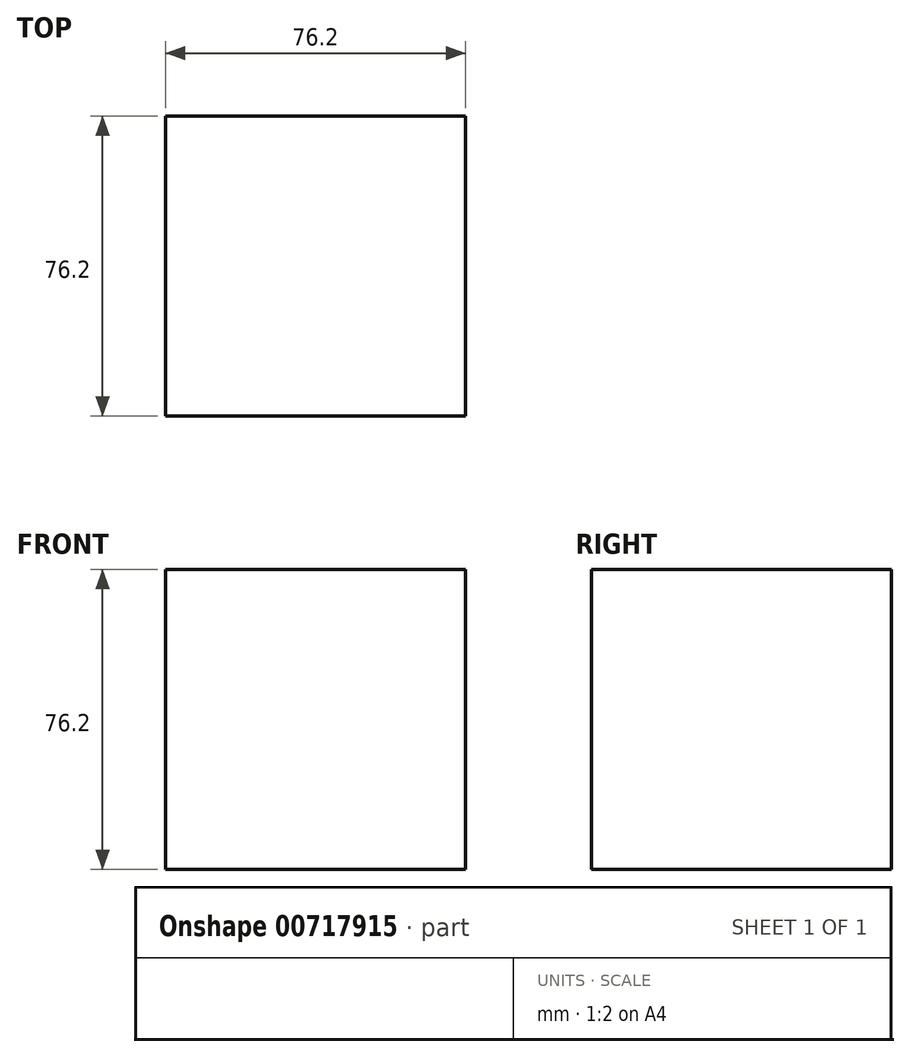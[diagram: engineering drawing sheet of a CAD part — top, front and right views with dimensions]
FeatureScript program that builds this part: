
annotation { "Feature Type Name" : "Feature", "Feature Type Description" : "" }
export const myFeature = defineFeature(function(context is Context, id is Id, definition is map)
    precondition{}
    {
        {
            var Q0;
            Q0=qCreatedBy(makeId("Front.planeOp"),FACE);
            var sketch = newSketch(context, id + "F0", { "sketchPlane" : qUnion([Q0])});
            skLineSegment(sketch, "E0.bottom", {"start": v(-25.54, 34.9) * mm, "end": v(50.66, 34.9) * mm});
            skLineSegment(sketch, "E0.top", {"start": v(-25.54, -41.3) * mm, "end": v(50.66, -41.3) * mm});
            skLineSegment(sketch, "E0.left", {"start": v(-25.54, 34.9) * mm, "end": v(-25.54, -41.3) * mm});
            skLineSegment(sketch, "E0.right", {"start": v(50.66, 34.9) * mm, "end": v(50.66, -41.3) * mm});
            skSolve(sketch);
        }
        {
            var Q0;
            Q0=makeQuery(id+"F0.imprint","IMPRINT",FACE,{"disambiguationData":[TD([[makeQuery(id+"F0.imprint","IMPRINT",EDGE,{"derivedFrom":sQuery(id+"F0.wireOp",EDGE,"E0.bottom")}),-1.0]])]});
            extrude(context, id + "F1", {"entities" : qUnion([Q0]), "depth" : 76.2 * mm, "offsetDistance" : 25.4 * mm});
        }
    });
